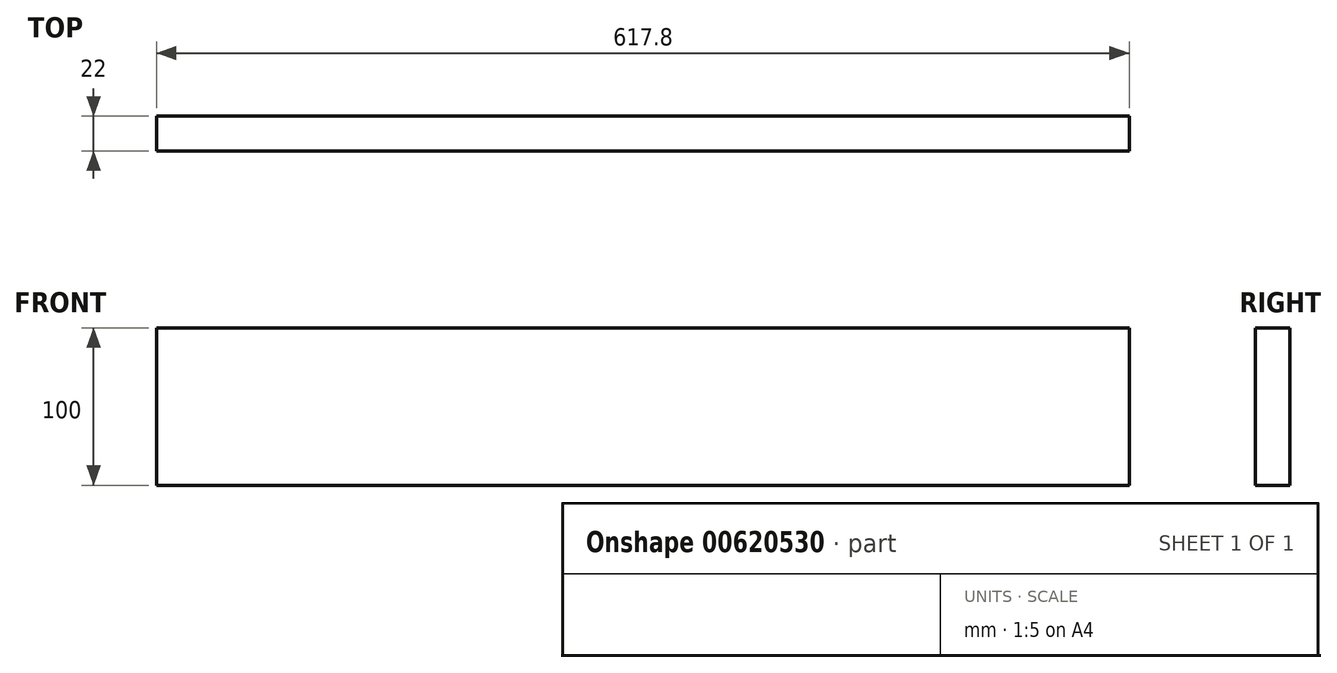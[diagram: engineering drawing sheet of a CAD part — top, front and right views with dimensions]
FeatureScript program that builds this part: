
annotation { "Feature Type Name" : "Feature", "Feature Type Description" : "" }
export const myFeature = defineFeature(function(context is Context, id is Id, definition is map)
    precondition{}
    {
        {
            var Q0;
            Q0=qCreatedBy(makeId("Front.planeOp"),FACE);
            var sketch = newSketch(context, id + "F0", { "sketchPlane" : qUnion([Q0])});
            skLineSegment(sketch, "E0.bottom", {"start": v(308.9, -50) * mm, "end": v(-308.9, -50) * mm});
            skLineSegment(sketch, "E0.top", {"start": v(308.9, 50) * mm, "end": v(-308.9, 50) * mm});
            skLineSegment(sketch, "E0.left", {"start": v(308.9, -50) * mm, "end": v(308.9, 50) * mm});
            skLineSegment(sketch, "E0.right", {"start": v(-308.9, -50) * mm, "end": v(-308.9, 50) * mm});
            skPoint(sketch, "E0.middle", {"position": v(0, 0) * mm});
            skSolve(sketch);
        }
        {
            var Q0;
            Q0 = qSketchRegion(id + "F0", true);
            extrude(context, id + "F1", {"entities" : qUnion([Q0]), "depth" : 22 * mm, "offsetDistance" : 25 * mm});
        }
    });
